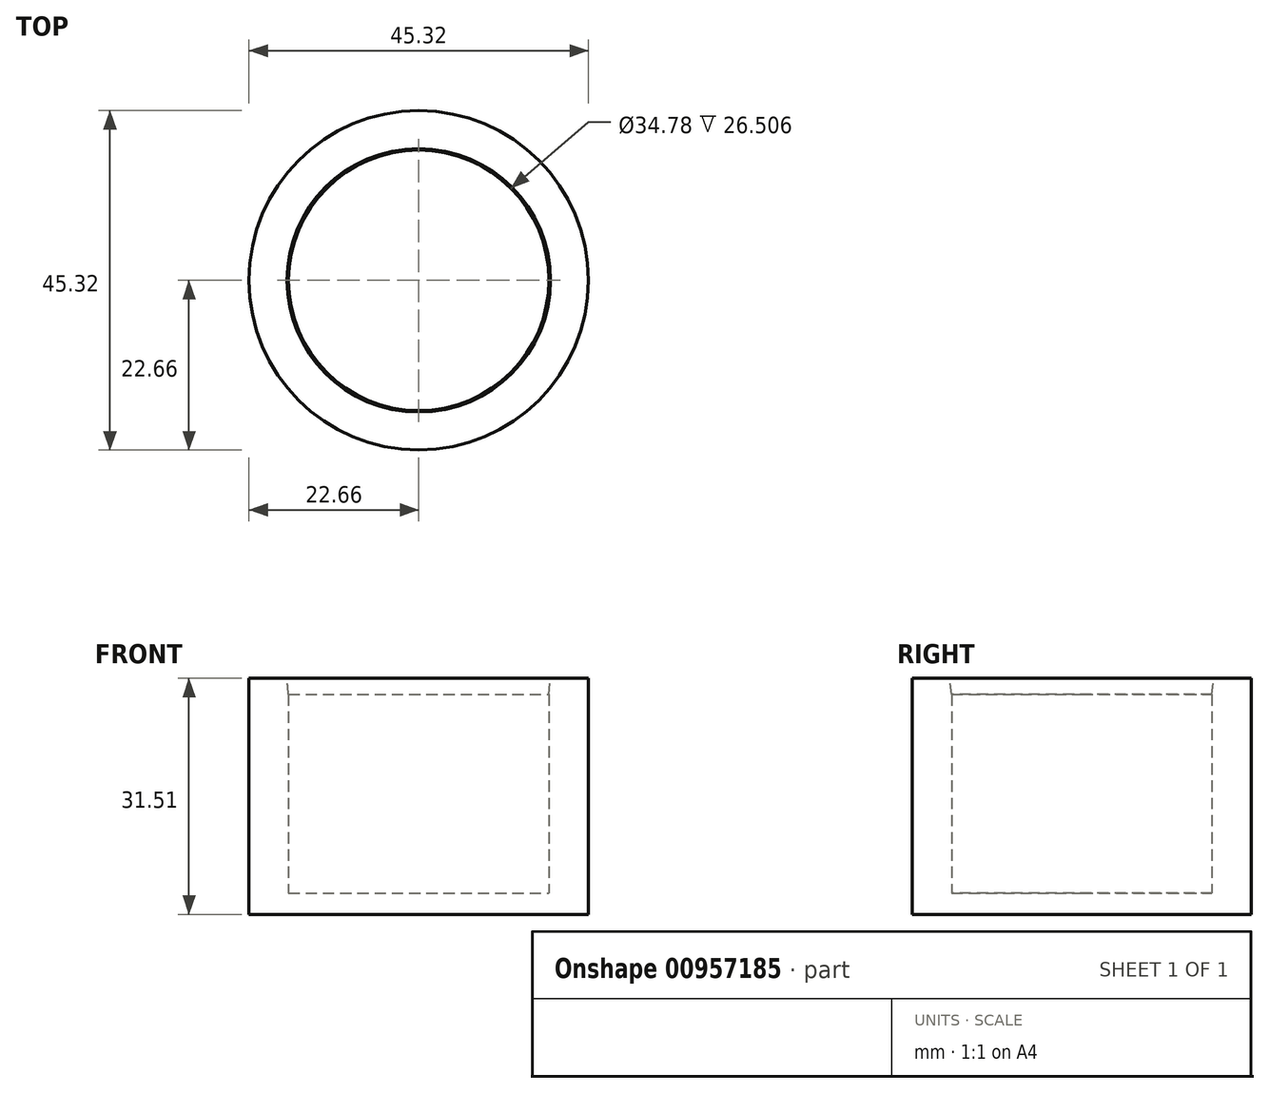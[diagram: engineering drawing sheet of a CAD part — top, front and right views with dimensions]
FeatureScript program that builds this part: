
annotation { "Feature Type Name" : "Feature", "Feature Type Description" : "" }
export const myFeature = defineFeature(function(context is Context, id is Id, definition is map)
    precondition{}
    {
        {
            var Q0;
            Q0=qCreatedBy(makeId("Front.planeOp"),FACE);
            var sketch = newSketch(context, id + "F0", { "sketchPlane" : qUnion([Q0])});
            skLineSegment(sketch, "E0", {"start": v(0, 0) * mm, "end": v(0, 72.12) * mm, "construction": true});
            skLineSegment(sketch, "E1", {"start": v(0, 0) * mm, "end": v(19.13, 0) * mm});
            skLineSegment(sketch, "E2", {"start": v(19.13, 0) * mm, "end": v(26.36, -7.63) * mm});
            skLineSegment(sketch, "E3", {"start": v(26.36, -7.63) * mm, "end": v(38.13, -7.63) * mm});
            skLineSegment(sketch, "E4", {"start": v(38.13, -7.63) * mm, "end": v(38.13, 68.37) * mm});
            skLineSegment(sketch, "E5", {"start": v(38.13, 68.37) * mm, "end": v(21.27, 75.33) * mm});
            skLineSegment(sketch, "E6", {"start": v(21.27, 75.33) * mm, "end": v(21.27, 91.01) * mm});
            skLineSegment(sketch, "E7", {"start": v(19.12, 91.01) * mm, "end": v(19.12, 71.76) * mm});
            skLineSegment(sketch, "E8", {"start": v(19.12, 71.76) * mm, "end": v(34.73, 65.32) * mm});
            skLineSegment(sketch, "E9", {"start": v(34.86, 65.63) * mm, "end": v(34.86, -4.58) * mm});
            skLineSegment(sketch, "E10", {"start": v(34.86, -4.58) * mm, "end": v(27.64, -4.58) * mm});
            skLineSegment(sketch, "E11", {"start": v(27.64, -4.58) * mm, "end": v(21.27, 2.98) * mm});
            skLineSegment(sketch, "E12", {"start": v(21.27, 2.98) * mm, "end": v(0, 2.98) * mm});
            skLineSegment(sketch, "E13", {"start": v(0, 2.98) * mm, "end": v(0, 0) * mm});
            skLineSegment(sketch, "E14", {"start": v(0, 0) * mm, "end": v(0, 2.98) * mm});
            skLineSegment(sketch, "E15", {"start": v(21.27, 91.01) * mm, "end": v(19.12, 91.01) * mm});
            skLineSegment(sketch, "E16", {"start": v(8.28, 0) * mm, "end": v(1.75, 0) * mm});
            skLineSegment(sketch, "E17", {"start": v(1.75, 0) * mm, "end": v(0, 2.98) * mm});
            skLineSegment(sketch, "E18", {"start": v(1.75, 0) * mm, "end": v(19.13, 0) * mm});
            skSolve(sketch);
        }
        {
            var Q0;
            Q0=qCreatedBy(makeId("Front.planeOp"),FACE);
            var sketch = newSketch(context, id + "F1", { "sketchPlane" : qUnion([Q0])});
            skLineSegment(sketch, "E19", {"start": v(0, 14.52) * mm, "end": v(22.66, 14.52) * mm});
            skLineSegment(sketch, "E20", {"start": v(22.66, 14.52) * mm, "end": v(22.66, 46.03) * mm});
            skLineSegment(sketch, "E21", {"start": v(22.66, 46.03) * mm, "end": v(17.6, 46.03) * mm});
            skLineSegment(sketch, "E22", {"start": v(17.39, 43.88) * mm, "end": v(17.39, 17.38) * mm});
            skLineSegment(sketch, "E23", {"start": v(17.39, 17.38) * mm, "end": v(0, 17.38) * mm});
            skLineSegment(sketch, "E24", {"start": v(0, 17.38) * mm, "end": v(0, 14.52) * mm});
            skLineSegment(sketch, "E25", {"start": v(17.39, 43.88) * mm, "end": v(17.6, 46.03) * mm});
            skSolve(sketch);
        }
        {
            var Q0;
            Q0 = qSketchRegion(id + "F1", true);
            var Q1;
            Q1=sQuery(id+"F0.wireOp",EDGE,"E0");
            revolve(context, id + "F2", {"surfaceOperationType" : NewSurfaceOperationType.NEW, "entities" : qUnion([Q0]), "axis" : qUnion([Q1]), "revolveType" : RevolveType.FULL});
        }
    });
